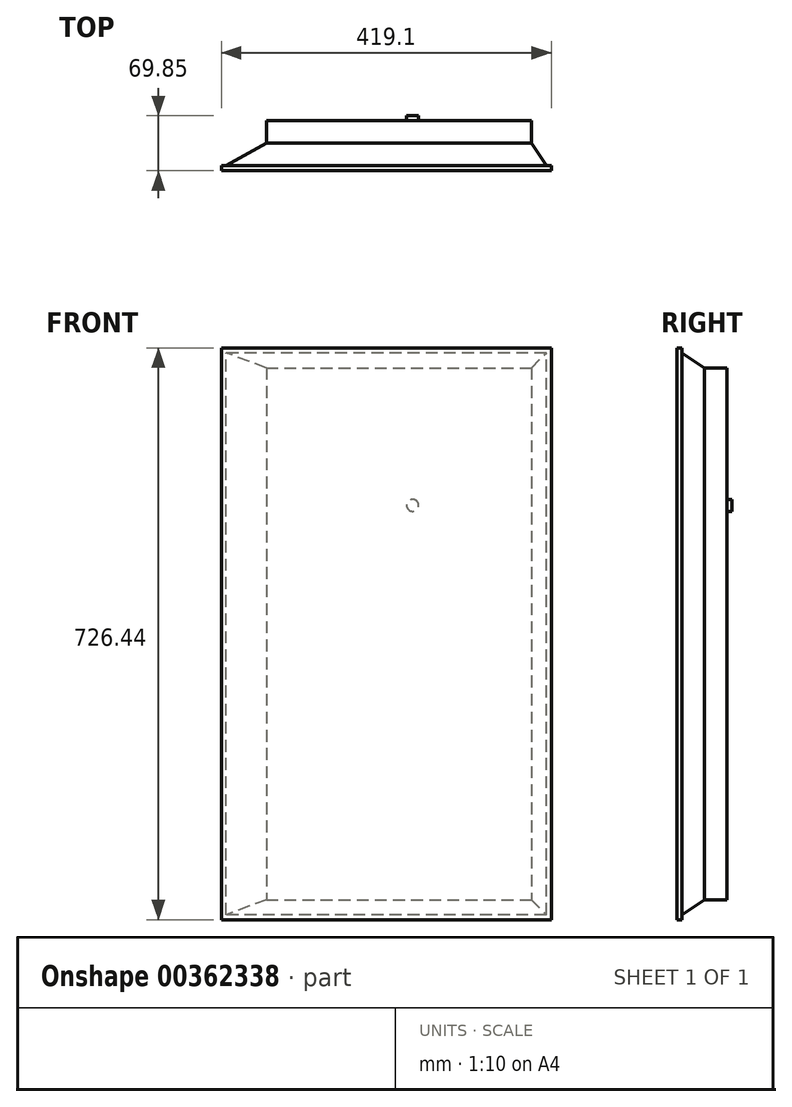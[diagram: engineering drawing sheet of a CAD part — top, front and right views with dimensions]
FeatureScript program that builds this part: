
annotation { "Feature Type Name" : "Feature", "Feature Type Description" : "" }
export const myFeature = defineFeature(function(context is Context, id is Id, definition is map)
    precondition{}
    {
        {
            var Q0;
            Q0=qCreatedBy(makeId("Front.planeOp"),FACE);
            var sketch = newSketch(context, id + "F0", { "sketchPlane" : qUnion([Q0])});
            skLineSegment(sketch, "E0.bottom", {"start": v(-209.55, 363.22) * mm, "end": v(209.55, 363.22) * mm});
            skLineSegment(sketch, "E0.top", {"start": v(-209.55, -363.22) * mm, "end": v(209.55, -363.22) * mm});
            skLineSegment(sketch, "E0.left", {"start": v(-209.55, 363.22) * mm, "end": v(-209.55, -363.22) * mm});
            skLineSegment(sketch, "E0.right", {"start": v(209.55, 363.22) * mm, "end": v(209.55, -363.22) * mm});
            skPoint(sketch, "E0.middle", {"position": v(0, 0) * mm});
            skSolve(sketch);
        }
        {
            var Q0;
            Q0=makeQuery(id+"F0.imprint","IMPRINT",FACE,{"disambiguationData":[TD([[makeQuery(id+"F0.imprint","IMPRINT",EDGE,{"derivedFrom":sQuery(id+"F0.wireOp",EDGE,"E0.bottom")}),-1.0]])]});
            extrude(context, id + "F1", {"entities" : qUnion([Q0]), "oppositeDirection" : true, "depth" : 6.35 * mm});
        }
        {
            var Q0;
            Q0=makeQuery(id+"F1.opExtrude","CAP_FACE",FACE,{"disambiguationData":[OSD([sQuery(id+"F0.wireOp",EDGE,"E0.bottom"),sQuery(id+"F0.wireOp",EDGE,"E0.top"),sQuery(id+"F0.wireOp",EDGE,"E0.left"),sQuery(id+"F0.wireOp",EDGE,"E0.right")])],"isStart":false});
            var sketch = newSketch(context, id + "F2", { "sketchPlane" : qUnion([Q0])});
            skLineSegment(sketch, "E1.bottom", {"start": v(107.55, 101.22) * mm, "end": v(-92.45, 101.22) * mm});
            skLineSegment(sketch, "E1.top", {"start": v(107.55, -98.78) * mm, "end": v(-92.45, -98.78) * mm});
            skLineSegment(sketch, "E1.left", {"start": v(107.55, 101.22) * mm, "end": v(107.55, -98.78) * mm});
            skLineSegment(sketch, "E1.right", {"start": v(-92.45, 101.22) * mm, "end": v(-92.45, -98.78) * mm});
            skPoint(sketch, "E1.middle", {"position": v(0, 0) * mm});
            skCircle(sketch, "E2", {"center": v(-92.45, 101.22) * mm, "radius": 6.35 * mm});
            skCircle(sketch, "E3", {"center": v(107.55, 101.22) * mm, "radius": 6.35 * mm});
            skCircle(sketch, "E4", {"center": v(107.55, -98.78) * mm, "radius": 6.35 * mm});
            skCircle(sketch, "E5", {"center": v(-92.45, -98.78) * mm, "radius": 6.35 * mm});
            skSolve(sketch);
        }
        {
            var Q0;
            Q0=makeQuery(id+"F1.opExtrude","CAP_FACE",FACE,{"disambiguationData":[OSD([sQuery(id+"F0.wireOp",EDGE,"E0.bottom"),sQuery(id+"F0.wireOp",EDGE,"E0.top"),sQuery(id+"F0.wireOp",EDGE,"E0.left"),sQuery(id+"F0.wireOp",EDGE,"E0.right")])],"isStart":false});
            var sketch = newSketch(context, id + "F3", { "sketchPlane" : qUnion([Q0])});
            skLineSegment(sketch, "E6.bottom", {"start": v(-167.2, 222.37) * mm, "end": v(-192.84, 222.37) * mm});
            skLineSegment(sketch, "E6.top", {"start": v(-167.2, 77.12) * mm, "end": v(-192.84, 77.12) * mm});
            skLineSegment(sketch, "E6.left", {"start": v(-167.2, 222.37) * mm, "end": v(-167.2, 77.12) * mm});
            skLineSegment(sketch, "E6.right", {"start": v(-192.84, 222.37) * mm, "end": v(-192.84, 77.12) * mm});
            skLineSegment(sketch, "E7.bottom", {"start": v(-167.2, -58.53) * mm, "end": v(-192.84, -58.53) * mm});
            skLineSegment(sketch, "E7.top", {"start": v(-167.2, -210.2) * mm, "end": v(-192.84, -210.2) * mm});
            skLineSegment(sketch, "E7.left", {"start": v(-167.2, -58.53) * mm, "end": v(-167.2, -210.2) * mm});
            skLineSegment(sketch, "E7.right", {"start": v(-192.84, -58.53) * mm, "end": v(-192.84, -210.2) * mm});
            skSolve(sketch);
        }
        {
            var Q0;
            {var subQ0=sQuery(id+"F2.wireOp",EDGE,"E1.left");var subQ1=sQuery(id+"F2.wireOp",EDGE,"E1.bottom");var subQ2=makeQuery(id+"F2.imprint","INTERSECT",VERTEX,{"derivedFrom":[subQ1,subQ0]});Q0=makeQuery(id+"F2.imprint","IMPRINT",FACE,{"disambiguationData":[TD([[makeQuery(id+"F2.imprint","IMPRINT",EDGE,{"disambiguationData":[TD([[subQ2,-1.0]])],"derivedFrom":subQ1}),-1.0]])]});}
            var Q1;
            {var subQ0=sQuery(id+"F2.wireOp",EDGE,"E1.left");var subQ1=sQuery(id+"F2.wireOp",EDGE,"E1.bottom");var subQ2=makeQuery(id+"F2.imprint","INTERSECT",VERTEX,{"derivedFrom":[subQ1,subQ0]});Q1=makeQuery(id+"F2.imprint","IMPRINT",FACE,{"disambiguationData":[TD([[makeQuery(id+"F2.imprint","IMPRINT",EDGE,{"disambiguationData":[TD([[subQ2,-1.0]])],"derivedFrom":subQ1}),1.0]])]});}
            var Q2;
            {var subQ0=sQuery(id+"F2.wireOp",EDGE,"E1.right");var subQ1=sQuery(id+"F2.wireOp",EDGE,"E1.bottom");var subQ2=makeQuery(id+"F2.imprint","INTERSECT",VERTEX,{"derivedFrom":[subQ1,subQ0]});Q2=makeQuery(id+"F2.imprint","IMPRINT",FACE,{"disambiguationData":[TD([[makeQuery(id+"F2.imprint","IMPRINT",EDGE,{"disambiguationData":[TD([[subQ2,1.0]])],"derivedFrom":subQ1}),-1.0]])]});}
            var Q3;
            {var subQ0=sQuery(id+"F2.wireOp",EDGE,"E1.right");var subQ1=sQuery(id+"F2.wireOp",EDGE,"E1.bottom");var subQ2=makeQuery(id+"F2.imprint","INTERSECT",VERTEX,{"derivedFrom":[subQ1,subQ0]});Q3=makeQuery(id+"F2.imprint","IMPRINT",FACE,{"disambiguationData":[TD([[makeQuery(id+"F2.imprint","IMPRINT",EDGE,{"disambiguationData":[TD([[subQ2,1.0]])],"derivedFrom":subQ1}),1.0]])]});}
            var Q4;
            {var subQ0=sQuery(id+"F2.wireOp",EDGE,"E1.left");var subQ1=sQuery(id+"F2.wireOp",EDGE,"E1.top");var subQ2=makeQuery(id+"F2.imprint","INTERSECT",VERTEX,{"derivedFrom":[subQ1,subQ0]});Q4=makeQuery(id+"F2.imprint","IMPRINT",FACE,{"disambiguationData":[TD([[makeQuery(id+"F2.imprint","IMPRINT",EDGE,{"disambiguationData":[TD([[subQ2,-1.0]])],"derivedFrom":subQ1}),-1.0]])]});}
            var Q5;
            {var subQ0=sQuery(id+"F2.wireOp",EDGE,"E1.left");var subQ1=sQuery(id+"F2.wireOp",EDGE,"E1.top");var subQ2=makeQuery(id+"F2.imprint","INTERSECT",VERTEX,{"derivedFrom":[subQ1,subQ0]});Q5=makeQuery(id+"F2.imprint","IMPRINT",FACE,{"disambiguationData":[TD([[makeQuery(id+"F2.imprint","IMPRINT",EDGE,{"disambiguationData":[TD([[subQ2,-1.0]])],"derivedFrom":subQ1}),1.0]])]});}
            var Q6;
            {var subQ0=sQuery(id+"F2.wireOp",EDGE,"E1.right");var subQ1=sQuery(id+"F2.wireOp",EDGE,"E1.top");var subQ2=makeQuery(id+"F2.imprint","INTERSECT",VERTEX,{"derivedFrom":[subQ1,subQ0]});Q6=makeQuery(id+"F2.imprint","IMPRINT",FACE,{"disambiguationData":[TD([[makeQuery(id+"F2.imprint","IMPRINT",EDGE,{"disambiguationData":[TD([[subQ2,1.0]])],"derivedFrom":subQ1}),-1.0]])]});}
            var Q7;
            {var subQ0=sQuery(id+"F2.wireOp",EDGE,"E1.right");var subQ1=sQuery(id+"F2.wireOp",EDGE,"E1.top");var subQ2=makeQuery(id+"F2.imprint","INTERSECT",VERTEX,{"derivedFrom":[subQ1,subQ0]});Q7=makeQuery(id+"F2.imprint","IMPRINT",FACE,{"disambiguationData":[TD([[makeQuery(id+"F2.imprint","IMPRINT",EDGE,{"disambiguationData":[TD([[subQ2,1.0]])],"derivedFrom":subQ1}),1.0]])]});}
            extrude(context, id + "F4", {"entities" : qUnion([Q0, Q1, Q2, Q3, Q4, Q5, Q6, Q7]), "operationType" : NewBodyOperationType.ADD, "depth" : 44.45 * mm});
        }
        {
            var Q0;
            Q0=makeQuery(id+"F1.opExtrude","CAP_FACE",FACE,{"disambiguationData":[OSD([sQuery(id+"F0.wireOp",EDGE,"E0.bottom"),sQuery(id+"F0.wireOp",EDGE,"E0.top"),sQuery(id+"F0.wireOp",EDGE,"E0.left"),sQuery(id+"F0.wireOp",EDGE,"E0.right")])],"isStart":false});
            var sketch = newSketch(context, id + "F5", { "sketchPlane" : qUnion([Q0])});
            skCircle(sketch, "E8", {"center": v(-33.45, 163.22) * mm, "radius": 7.62 * mm});
            skSolve(sketch);
        }
        {
            var Q0;
            Q0 = qSketchRegion(id + "F5", true);
            extrude(context, id + "F6", {"entities" : qUnion([Q0]), "operationType" : NewBodyOperationType.ADD, "depth" : 63.5 * mm});
        }
        {
            var Q0;
            Q0=makeQuery(id+"F2.imprint","IMPRINT",FACE,{"disambiguationData":[TD([[makeQuery(id+"F2.imprint","IMPRINT",EDGE,{"derivedFrom":makeQuery(id+"F1.opExtrude","CAP_EDGE",EDGE,{"disambiguationData":[OSD([sQuery(id+"F0.wireOp",EDGE,"E0.bottom")])],"isStart":false})}),1.0]])]});
            cPlane(context, id + "F7", {"entities" : qUnion([Q0]), "cplaneType" : CPlaneType.OFFSET, "offset" : 28.57 * mm, "width" : 152.4 * mm, "height" : 152.4 * mm});
        }
        {
            var Q0;
            Q0=qCreatedBy(id+"F7.planeOp",FACE);
            var sketch = newSketch(context, id + "F8", { "sketchPlane" : qUnion([Q0])});
            skLineSegment(sketch, "E9.bottom", {"start": v(152.4, 337.82) * mm, "end": v(-184.15, 337.82) * mm});
            skLineSegment(sketch, "E9.top", {"start": v(152.4, -337.82) * mm, "end": v(-184.15, -337.82) * mm});
            skLineSegment(sketch, "E9.left", {"start": v(152.4, 337.82) * mm, "end": v(152.4, -337.82) * mm});
            skLineSegment(sketch, "E9.right", {"start": v(-184.15, 337.82) * mm, "end": v(-184.15, -337.82) * mm});
            skSolve(sketch);
        }
        {
            var Q0;
            Q0=makeQuery(id+"F2.imprint","IMPRINT",FACE,{"disambiguationData":[TD([[makeQuery(id+"F2.imprint","IMPRINT",EDGE,{"derivedFrom":makeQuery(id+"F1.opExtrude","CAP_EDGE",EDGE,{"disambiguationData":[OSD([sQuery(id+"F0.wireOp",EDGE,"E0.bottom")])],"isStart":false})}),1.0]])]});
            var sketch = newSketch(context, id + "F9", { "sketchPlane" : qUnion([Q0])});
            skLineSegment(sketch, "E10.bottom", {"start": v(-203.2, -356.87) * mm, "end": v(203.2, -356.87) * mm});
            skLineSegment(sketch, "E10.top", {"start": v(-203.2, 356.87) * mm, "end": v(203.2, 356.87) * mm});
            skLineSegment(sketch, "E10.left", {"start": v(-203.2, -356.87) * mm, "end": v(-203.2, 356.87) * mm});
            skLineSegment(sketch, "E10.right", {"start": v(203.2, -356.87) * mm, "end": v(203.2, 356.87) * mm});
            skSolve(sketch);
        }
        {
            var Q1;
            Q1 = qSketchRegion(id + "F8", true);
            var Q2;
            Q2 = qSketchRegion(id + "F9", true);
            loft(context, id + "F10", {"operationType" : NewBodyOperationType.ADD, "sheetProfilesArray" : [{ "sheetProfileEntities" : qUnion([Q1]) }, { "sheetProfileEntities" : qUnion([Q2]) }]});
        }
        {
            var Q0;
            Q0 = qSketchRegion(id + "F8", true);
            extrude(context, id + "F11", {"entities" : qUnion([Q0]), "operationType" : NewBodyOperationType.ADD, "depth" : 28.57 * mm});
        }
    });
